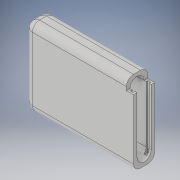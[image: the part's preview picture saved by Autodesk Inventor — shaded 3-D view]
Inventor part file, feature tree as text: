
AUTODESK INVENTOR PART (.ipt)
format: ipt  version: 2018 (Build 220112000, 112)  size: 187,392 bytes
history: native  units: in
note: dims shown in document units (in); Inventor stores cm internally (conversion verified against a paired STEP export)
features: sketch x4, extrude x4, fillet x1, projected_geometry x1
ambient origin geometry x8: Origin, YZ Plane, XZ Plane, XY Plane, X Axis, Y Axis, Z Axis, Center Point
bodies: Solid1 (feature_tree)
feature tree (10):
  sketch  "Sketch1"  dims[d0=3.45in d1=2.5in]
  extrude  "Extrusion1"  Depth=2.5in
  extrude  "Extrusion2"  Depth=0.125in
  fillet  "Fillet1"  Radius=2.625in
  extrude  "Extrusion3"  Depth=0.75in TaperAngle=0.0deg
  extrude  "Extrusion4"  Depth=0.25in
  sketch  "Sketch2"  dims[d2=0.125in d3=0.125in d4=2.625in]
  sketch  "Sketch3"  dims[d6=0.0in d7=0.75in d8=0.0in]
  projected_geometry  "Projected Loop1"
  sketch  "Sketch4"  dims[d9=0.5in d10=0.0in d11=0.25in d12=0.25in d13=0.0in d14=0.1in d15=0.0625in d16=0.075in d17=2.2in d18=0.0in]
